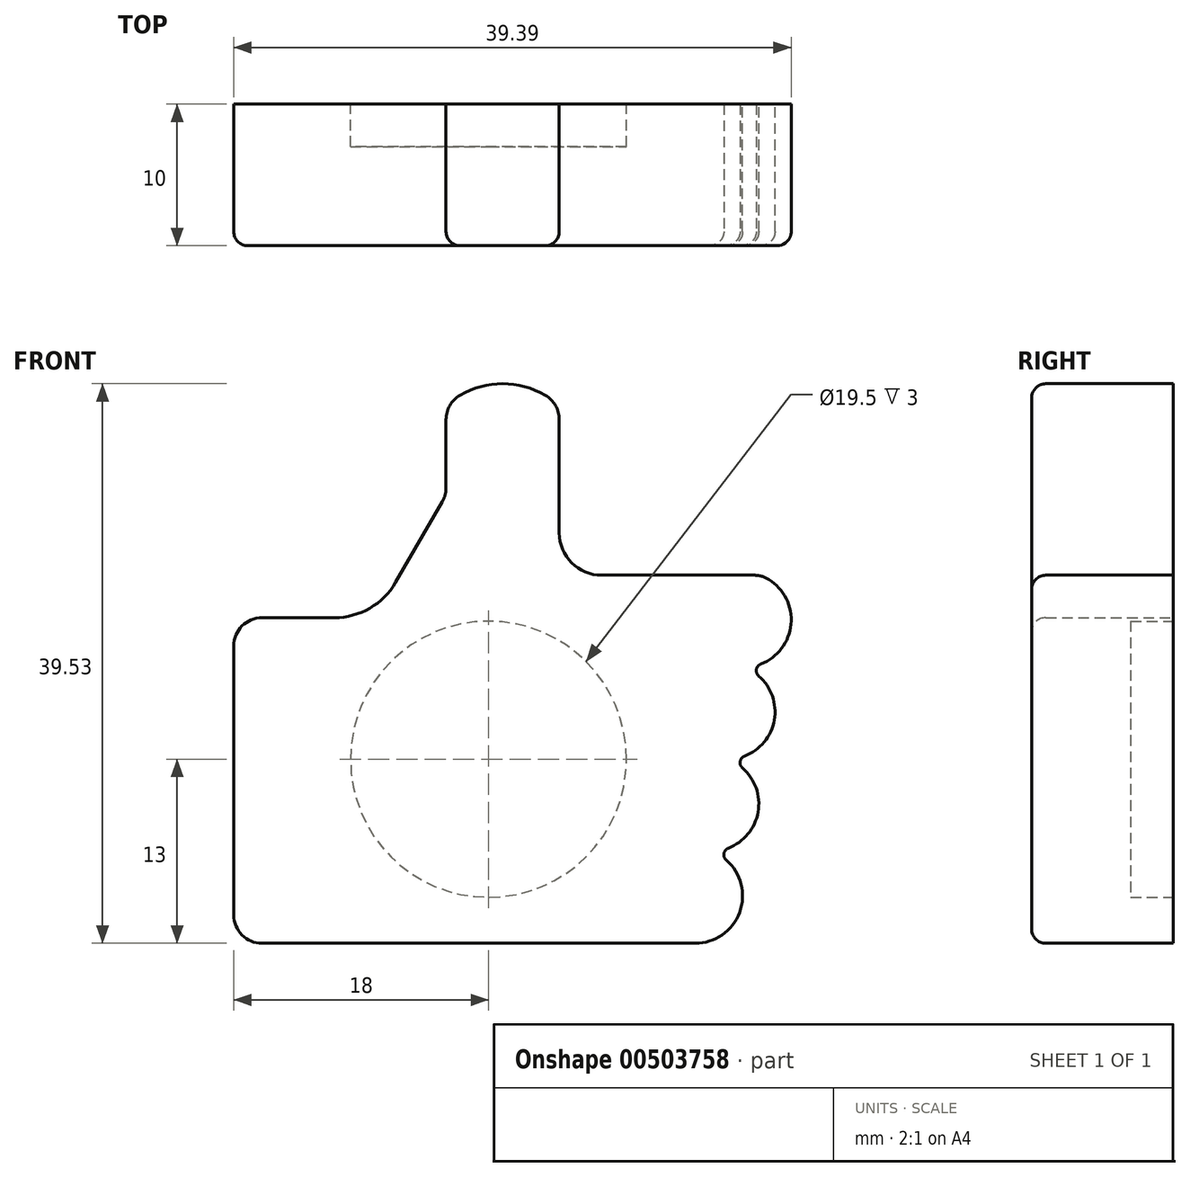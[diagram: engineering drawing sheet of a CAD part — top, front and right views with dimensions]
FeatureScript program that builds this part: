
annotation { "Feature Type Name" : "Feature", "Feature Type Description" : "" }
export const myFeature = defineFeature(function(context is Context, id is Id, definition is map)
    precondition{}
    {
        {
            var Q0;
            Q0=qCreatedBy(makeId("Front.planeOp"),FACE);
            var sketch = newSketch(context, id + "F0", { "sketchPlane" : qUnion([Q0])});
            skLineSegment(sketch, "E0", {"start": v(0, 0) * mm, "end": v(0, 23) * mm});
            skLineSegment(sketch, "E1", {"start": v(0, 23) * mm, "end": v(7.11, 23) * mm});
            skLineSegment(sketch, "E2", {"start": v(11.44, 25.5) * mm, "end": v(15, 31.66) * mm});
            skLineSegment(sketch, "E3", {"start": v(23, 38) * mm, "end": v(23, 29) * mm});
            skLineSegment(sketch, "E4", {"start": v(26, 26) * mm, "end": v(37.19, 26) * mm});
            skLineSegment(sketch, "E5", {"start": v(37.19, 26) * mm, "end": v(32.6, 0) * mm, "construction": true});
            skLineSegment(sketch, "E6", {"start": v(32.6, 0) * mm, "end": v(0, 0) * mm});
            skArc(sketch, "E7", {"start": v(36.04, 19.5) * mm, "mid": v(39.34, 22.27) * mm, "end": v(37.19, 26) * mm});
            skArc(sketch, "E8", {"start": v(34.9, 13) * mm, "mid": v(38.2, 15.77) * mm, "end": v(36.04, 19.5) * mm});
            skArc(sketch, "E9", {"start": v(33.75, 6.5) * mm, "mid": v(37.05, 9.27) * mm, "end": v(34.9, 13) * mm});
            skArc(sketch, "E10", {"start": v(32.6, 0) * mm, "mid": v(35.9, 2.77) * mm, "end": v(33.75, 6.5) * mm});
            skLineSegment(sketch, "E11", {"start": v(35.42, 0) * mm, "end": v(40, 26) * mm, "construction": true});
            skPoint(sketch, "E12.visualSharp", {"position": v(10, 23) * mm});
            skArc(sketch, "E12.filletArc", {"start": v(7.11, 23) * mm, "mid": v(9.61, 23.67) * mm, "end": v(11.44, 25.5) * mm});
            skPoint(sketch, "E13.visualSharp", {"position": v(23, 26) * mm});
            skArc(sketch, "E13.filletArc", {"start": v(23, 29) * mm, "mid": v(23.88, 26.88) * mm, "end": v(26, 26) * mm});
            skLineSegment(sketch, "E14", {"start": v(15, 31.66) * mm, "end": v(15, 38) * mm});
            skLineSegment(sketch, "E15", {"start": v(15, 38) * mm, "end": v(23, 38) * mm, "construction": true});
            skArc(sketch, "E16", {"start": v(23, 38) * mm, "mid": v(19, 39.53) * mm, "end": v(15, 38) * mm});
            skSolve(sketch);
        }
        {
            var Q0;
            Q0=makeQuery(id+"F0.imprint","IMPRINT",FACE,{"disambiguationData":[TD([[makeQuery(id+"F0.imprint","IMPRINT",EDGE,{"derivedFrom":sQuery(id+"F0.wireOp",EDGE,"E0")}),-1.0]])]});
            extrude(context, id + "F1", {"entities" : qUnion([Q0]), "depth" : 10 * mm, "offsetDistance" : 25 * mm});
        }
        {
            var Q0;
            Q0=makeQuery(id+"F1.opExtrude","SWEPT_EDGE",EDGE,{"disambiguationData":[OSD([sQuery(id+"F0.wireOp",EDGE,"E4"),sQuery(id+"F0.wireOp",EDGE,"E7")])]});
            var Q1;
            Q1=makeQuery(id+"F1.opExtrude","SWEPT_EDGE",EDGE,{"disambiguationData":[OSD([sQuery(id+"F0.wireOp",EDGE,"E3"),sQuery(id+"F0.wireOp",EDGE,"E16")])]});
            var Q2;
            Q2=makeQuery(id+"F1.opExtrude","SWEPT_EDGE",EDGE,{"disambiguationData":[OSD([sQuery(id+"F0.wireOp",EDGE,"E14"),sQuery(id+"F0.wireOp",EDGE,"E16")])]});
            var Q3;
            Q3=makeQuery(id+"F1.opExtrude","SWEPT_EDGE",EDGE,{"disambiguationData":[OSD([sQuery(id+"F0.wireOp",EDGE,"E2"),sQuery(id+"F0.wireOp",EDGE,"E14")])]});
            var Q4;
            Q4=makeQuery(id+"F1.opExtrude","SWEPT_EDGE",EDGE,{"disambiguationData":[OSD([sQuery(id+"F0.wireOp",EDGE,"E0"),sQuery(id+"F0.wireOp",EDGE,"E1")])]});
            var Q5;
            Q5=makeQuery(id+"F1.opExtrude","SWEPT_EDGE",EDGE,{"disambiguationData":[OSD([sQuery(id+"F0.wireOp",EDGE,"E0"),sQuery(id+"F0.wireOp",EDGE,"E6")])]});
            fillet(context, id + "F2", {"entities" : qUnion([Q0, Q1, Q2, Q3, Q4, Q5]), "radius" : 2 * mm, "tangentPropagation" : true, "allowEdgeOverflow" : false});
        }
        {
            var Q0;
            Q0=makeQuery(id+"F1.opExtrude","CAP_FACE",FACE,{"disambiguationData":[OSD([sQuery(id+"F0.wireOp",EDGE,"E0"),sQuery(id+"F0.wireOp",EDGE,"E1"),sQuery(id+"F0.wireOp",EDGE,"E2"),sQuery(id+"F0.wireOp",EDGE,"E3"),sQuery(id+"F0.wireOp",EDGE,"E4"),sQuery(id+"F0.wireOp",EDGE,"E6"),sQuery(id+"F0.wireOp",EDGE,"E7"),sQuery(id+"F0.wireOp",EDGE,"E8"),sQuery(id+"F0.wireOp",EDGE,"E9"),sQuery(id+"F0.wireOp",EDGE,"E10"),sQuery(id+"F0.wireOp",EDGE,"E12.filletArc"),sQuery(id+"F0.wireOp",EDGE,"E13.filletArc"),sQuery(id+"F0.wireOp",EDGE,"E14"),sQuery(id+"F0.wireOp",EDGE,"E16")])],"isStart":true});
            var sketch = newSketch(context, id + "F3", { "sketchPlane" : qUnion([Q0])});
            skCircle(sketch, "E17", {"center": v(-18, 13) * mm, "radius": 9.75 * mm});
            skSolve(sketch);
        }
        {
            var Q0;
            Q0=makeQuery(id+"F3.imprint","IMPRINT",FACE,{"disambiguationData":[TD([[makeQuery(id+"F3.imprint","IMPRINT",EDGE,{"derivedFrom":sQuery(id+"F3.wireOp",EDGE,"E17")}),1.0]])]});
            extrude(context, id + "F4", {"entities" : qUnion([Q0]), "operationType" : NewBodyOperationType.REMOVE, "oppositeDirection" : true, "depth" : 3 * mm, "offsetDistance" : 25 * mm});
        }
        {
            var Q0;
            Q0=makeQuery(id+"F1.opExtrude","SWEPT_EDGE",EDGE,{"disambiguationData":[OSD([sQuery(id+"F0.wireOp",EDGE,"E9"),sQuery(id+"F0.wireOp",EDGE,"E10")])]});
            var Q1;
            Q1=makeQuery(id+"F1.opExtrude","SWEPT_EDGE",EDGE,{"disambiguationData":[OSD([sQuery(id+"F0.wireOp",EDGE,"E8"),sQuery(id+"F0.wireOp",EDGE,"E9")])]});
            var Q2;
            Q2=makeQuery(id+"F1.opExtrude","SWEPT_EDGE",EDGE,{"disambiguationData":[OSD([sQuery(id+"F0.wireOp",EDGE,"E7"),sQuery(id+"F0.wireOp",EDGE,"E8")])]});
            fillet(context, id + "F5", {"entities" : qUnion([Q0, Q1, Q2]), "radius" : .5 * mm, "tangentPropagation" : true, "allowEdgeOverflow" : false});
        }
        {
            var Q0;
            Q0=makeQuery(id+"F1.opExtrude","CAP_FACE",FACE,{"disambiguationData":[OSD([sQuery(id+"F0.wireOp",EDGE,"E0"),sQuery(id+"F0.wireOp",EDGE,"E1"),sQuery(id+"F0.wireOp",EDGE,"E2"),sQuery(id+"F0.wireOp",EDGE,"E3"),sQuery(id+"F0.wireOp",EDGE,"E4"),sQuery(id+"F0.wireOp",EDGE,"E6"),sQuery(id+"F0.wireOp",EDGE,"E7"),sQuery(id+"F0.wireOp",EDGE,"E8"),sQuery(id+"F0.wireOp",EDGE,"E9"),sQuery(id+"F0.wireOp",EDGE,"E10"),sQuery(id+"F0.wireOp",EDGE,"E12.filletArc"),sQuery(id+"F0.wireOp",EDGE,"E13.filletArc"),sQuery(id+"F0.wireOp",EDGE,"E14"),sQuery(id+"F0.wireOp",EDGE,"E16")])],"isStart":false});
            fillet(context, id + "F6", {"entities" : qUnion([Q0]), "radius" : 1 * mm, "tangentPropagation" : true, "allowEdgeOverflow" : false});
        }
    });
